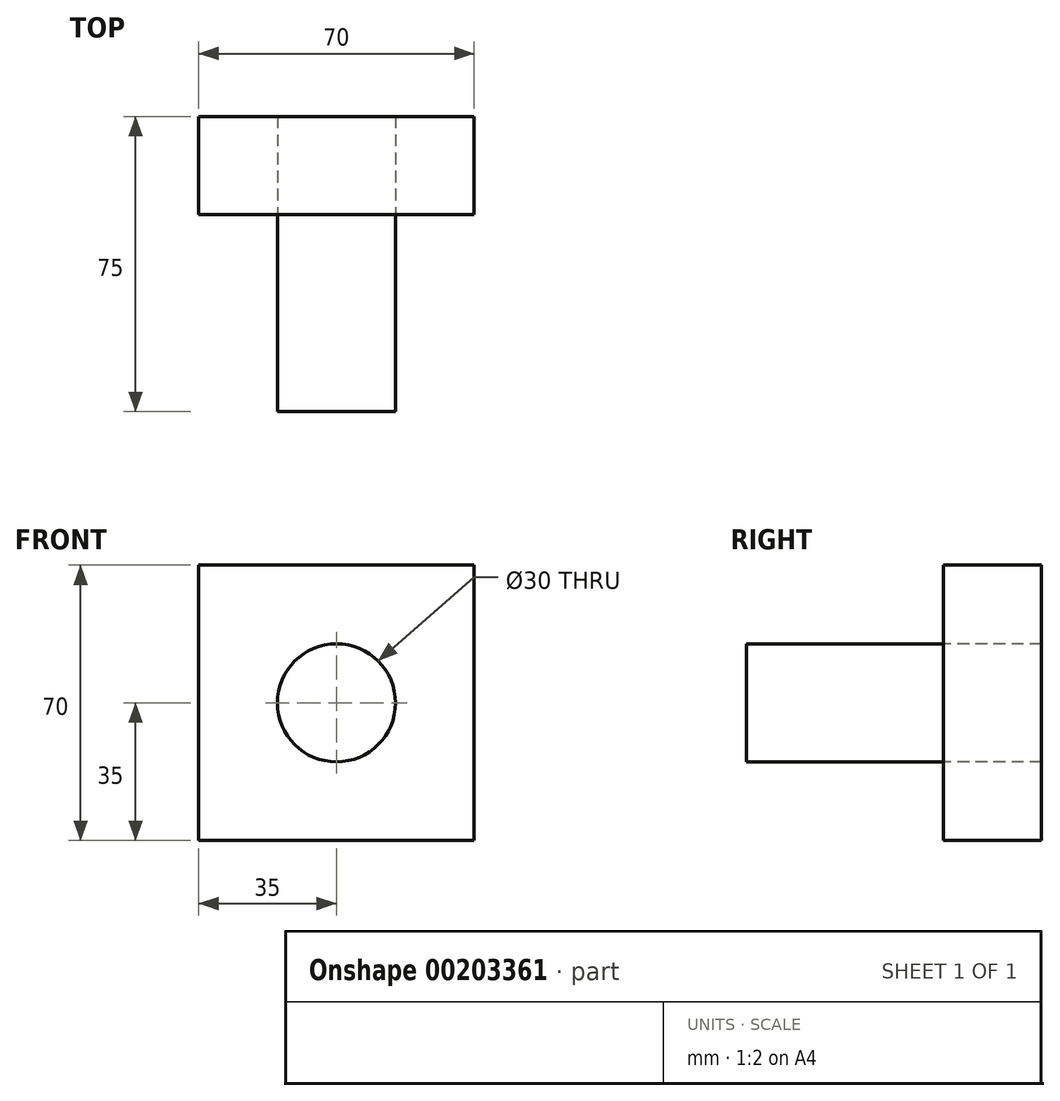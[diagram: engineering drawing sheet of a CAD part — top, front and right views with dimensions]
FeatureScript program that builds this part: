
annotation { "Feature Type Name" : "Feature", "Feature Type Description" : "" }
export const myFeature = defineFeature(function(context is Context, id is Id, definition is map)
    precondition{}
    {
        {
            var Q0;
            Q0=qCreatedBy(makeId("Front.planeOp"),FACE);
            var sketch = newSketch(context, id + "F0", { "sketchPlane" : qUnion([Q0])});
            skCircle(sketch, "E0", {"center": v(0, 0) * mm, "radius": 15 * mm});
            skSolve(sketch);
        }
        {
            var Q0;
            Q0=makeQuery(id+"F0.imprint","IMPRINT",FACE,{"disambiguationData":[TD([[makeQuery(id+"F0.imprint","IMPRINT",EDGE,{"derivedFrom":sQuery(id+"F0.wireOp",EDGE,"E0")}),1.0]])]});
            extrude(context, id + "F1", {"entities" : qUnion([Q0]), "depth" : 50 * mm, "offsetDistance" : 25 * mm});
        }
        {
            var Q0;
            Q0=makeQuery(id+"F1.opExtrude","CAP_FACE",FACE,{"disambiguationData":[OSD([sQuery(id+"F0.wireOp",EDGE,"E0")])],"isStart":true});
            var sketch = newSketch(context, id + "F2", { "sketchPlane" : qUnion([Q0])});
            skLineSegment(sketch, "E1.bottom", {"start": v(35, -35) * mm, "end": v(-35, -35) * mm});
            skLineSegment(sketch, "E1.top", {"start": v(35, 35) * mm, "end": v(-35, 35) * mm});
            skLineSegment(sketch, "E1.left", {"start": v(35, -35) * mm, "end": v(35, 35) * mm});
            skLineSegment(sketch, "E1.right", {"start": v(-35, -35) * mm, "end": v(-35, 35) * mm});
            skPoint(sketch, "E1.middle", {"position": v(0, 0) * mm});
            skSolve(sketch);
        }
        {
            var Q0;
            Q0=makeQuery(id+"F2.imprint","IMPRINT",FACE,{"disambiguationData":[TD([[makeQuery(id+"F2.imprint","IMPRINT",EDGE,{"derivedFrom":sQuery(id+"F2.wireOp",EDGE,"E1.bottom")}),-1.0]])]});
            extrude(context, id + "F3", {"entities" : qUnion([Q0]), "depth" : 25 * mm, "offsetDistance" : 25 * mm});
        }
    });
